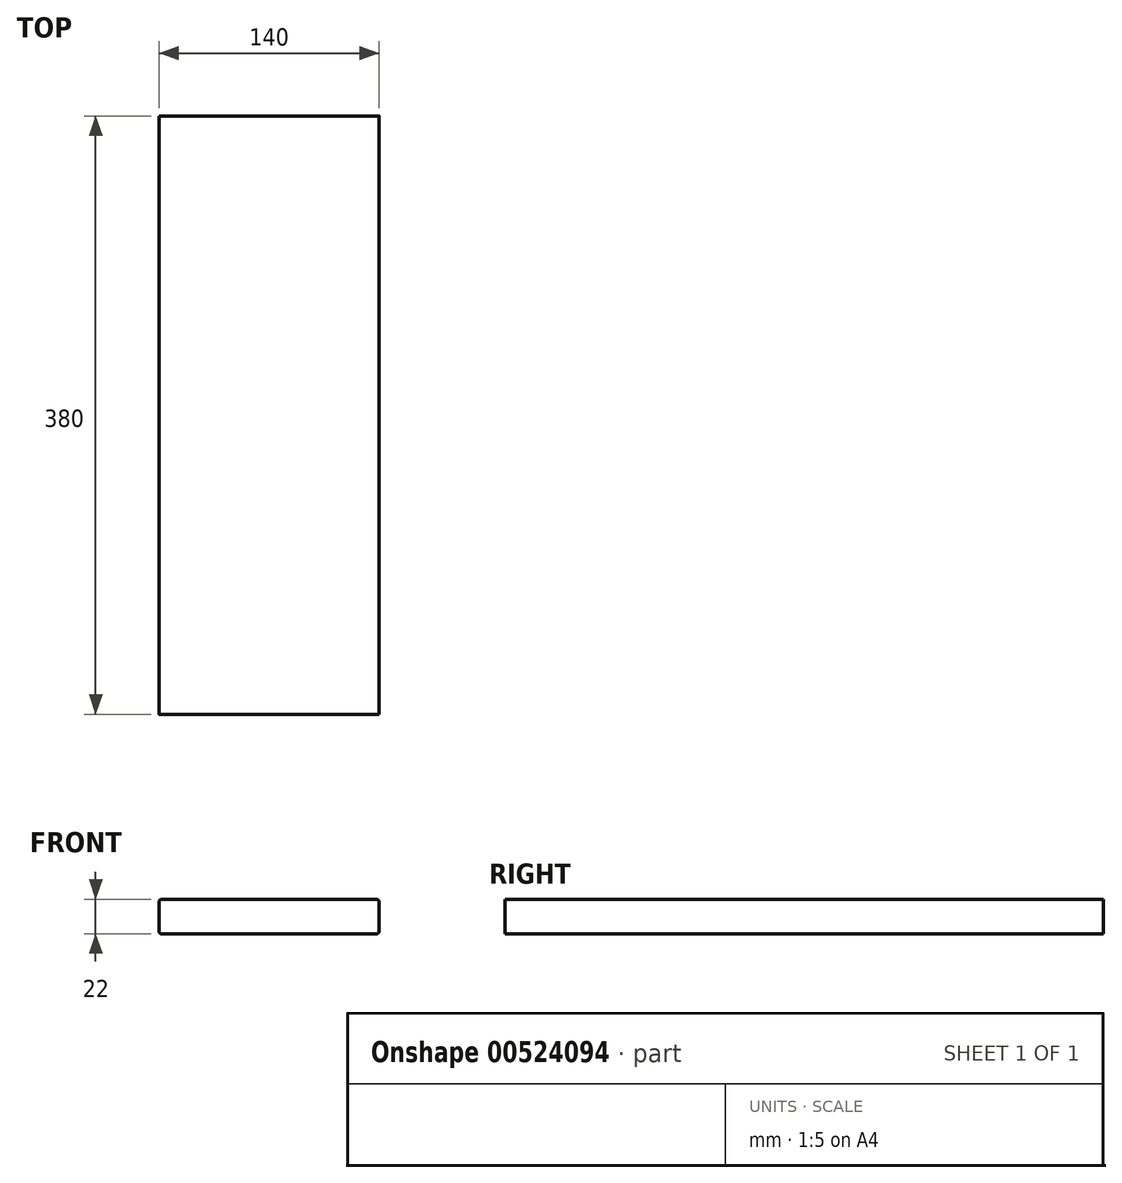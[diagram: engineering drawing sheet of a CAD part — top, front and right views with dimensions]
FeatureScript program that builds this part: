
annotation { "Feature Type Name" : "Feature", "Feature Type Description" : "" }
export const myFeature = defineFeature(function(context is Context, id is Id, definition is map)
    precondition{}
    {
        {
            var Q0;
            Q0=qCreatedBy(makeId("Front.planeOp"),FACE);
            var sketch = newSketch(context, id + "F0", { "sketchPlane" : qUnion([Q0])});
            skLineSegment(sketch, "E0.bottom", {"start": v(-70, 11) * mm, "end": v(70, 11) * mm});
            skLineSegment(sketch, "E0.top", {"start": v(-70, -11) * mm, "end": v(70, -11) * mm});
            skLineSegment(sketch, "E0.left", {"start": v(-70, 11) * mm, "end": v(-70, -11) * mm});
            skLineSegment(sketch, "E0.right", {"start": v(70, 11) * mm, "end": v(70, -11) * mm});
            skSolve(sketch);
        }
        {
            var Q0;
            Q0=qSketchRegion(id+"F0",true);
            extrude(context, id + "F1", {"entities" : qUnion([Q0]), "endBound" : BoundingType.SYMMETRIC, "depth" : 380 * mm, "offsetDistance" : 25 * mm});
        }
        {
            var Q0;
            Q0=makeQuery(id+"F1.opExtrude","SWEPT_EDGE",EDGE,{"disambiguationData":[OSD([sQuery(id+"F0.wireOp",EDGE,"E0.bottom"),sQuery(id+"F0.wireOp",EDGE,"E0.right")])]});
            var Q1;
            Q1=makeQuery(id+"F1.opExtrude","SWEPT_EDGE",EDGE,{"disambiguationData":[OSD([sQuery(id+"F0.wireOp",EDGE,"E0.top"),sQuery(id+"F0.wireOp",EDGE,"E0.right")])]});
            var Q2;
            Q2=makeQuery(id+"F1.opExtrude","SWEPT_EDGE",EDGE,{"disambiguationData":[OSD([sQuery(id+"F0.wireOp",EDGE,"E0.top"),sQuery(id+"F0.wireOp",EDGE,"E0.left")])]});
            var Q3;
            Q3=makeQuery(id+"F1.opExtrude","SWEPT_EDGE",EDGE,{"disambiguationData":[OSD([sQuery(id+"F0.wireOp",EDGE,"E0.bottom"),sQuery(id+"F0.wireOp",EDGE,"E0.left")])]});
            fillet(context, id + "F2", {"entities" : qUnion([Q0, Q1, Q2, Q3]), "radius" : 2 * mm, "tangentPropagation" : true, "allowEdgeOverflow" : false});
        }
    });
